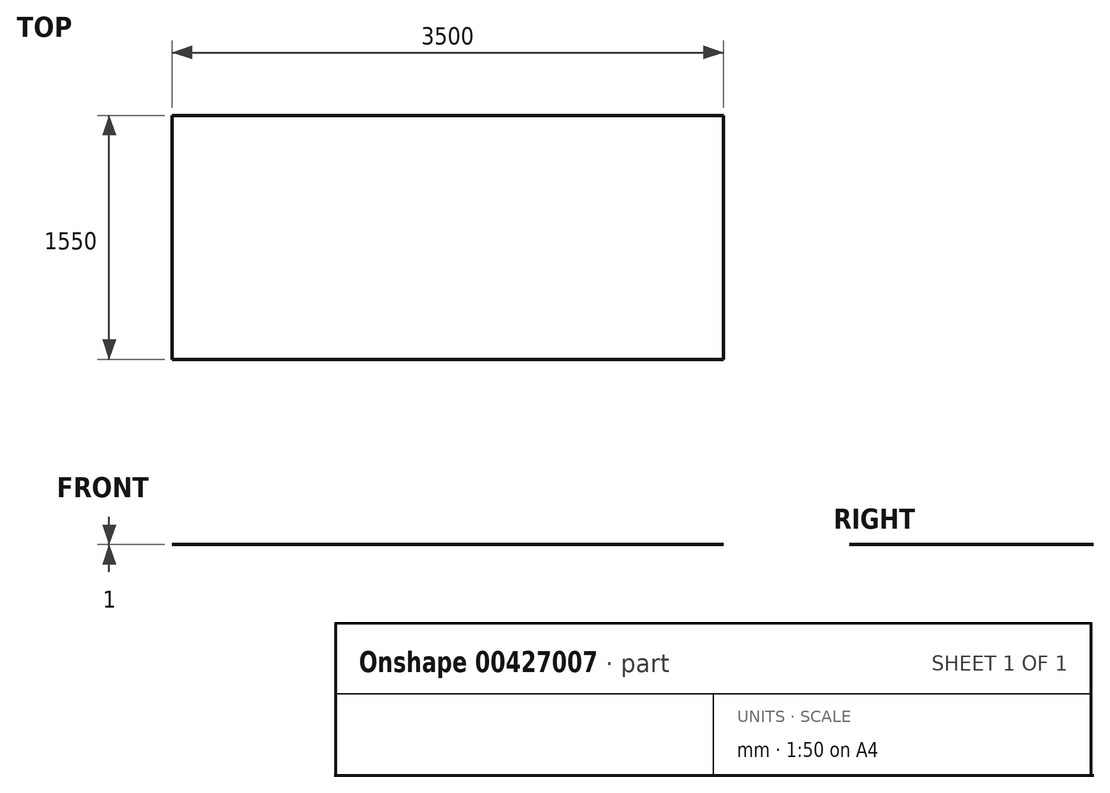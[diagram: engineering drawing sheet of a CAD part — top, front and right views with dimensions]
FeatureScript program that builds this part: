
annotation { "Feature Type Name" : "Feature", "Feature Type Description" : "" }
export const myFeature = defineFeature(function(context is Context, id is Id, definition is map)
    precondition{}
    {
        {
            var Q0;
            Q0=qCreatedBy(makeId("Right.planeOp"),FACE);
            var sketch = newSketch(context, id + "F0", { "sketchPlane" : qUnion([Q0])});
            skLineSegment(sketch, "E0.bottom", {"start": v(0, 0) * mm, "end": v(1550, 0) * mm});
            skLineSegment(sketch, "E0.top", {"start": v(0, 1) * mm, "end": v(1550, 1) * mm});
            skLineSegment(sketch, "E0.left", {"start": v(0, 0) * mm, "end": v(0, 1) * mm});
            skLineSegment(sketch, "E0.right", {"start": v(1550, 0) * mm, "end": v(1550, 1) * mm});
            skSolve(sketch);
        }
        {
            var Q0;
            Q0=makeQuery(id+"F0.imprint","IMPRINT",FACE,{"disambiguationData":[TD([[makeQuery(id+"F0.imprint","IMPRINT",EDGE,{"derivedFrom":sQuery(id+"F0.wireOp",EDGE,"E0.bottom")}),1.0]])]});
            extrude(context, id + "F1", {"entities" : qUnion([Q0]), "depth" : 3500 * mm});
        }
    });
